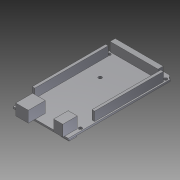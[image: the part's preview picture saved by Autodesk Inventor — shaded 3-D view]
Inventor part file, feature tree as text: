
AUTODESK INVENTOR PART (.ipt)
format: ipt  version: 2011 SP2 (Build 150309200, 309)  size: 225,792 bytes
history: native  units: mm
features: extrude x6, projected_geometry x5, sketch x3
ambient origin geometry x8: Origin, YZ Plane, XZ Plane, XY Plane, X Axis, Y Axis, Z Axis, Center Point
bodies: Solid1 (feature_tree)
feature tree (14):
  extrude  "Extrusion1"  Depth=1.7mm
  sketch  "Sketch3"  dims[d2=53.3mm d3=0.0mm d23=9.1mm]
  extrude  "Extrusion3"  Depth=9.1mm
  extrude  "Extrusion9"  Depth=16.4mm
  extrude  "Extrusion10"  Depth=12.2mm
  sketch  "Sketch7"  dims[d24=9.75mm d25=16.4mm d26=12.2mm d27=8.8mm d28=14.0mm d29=12.4mm d30=1.7mm d31=10.8mm d32=0.0mm d44=3.0mm d45=3.4mm d46=3.0mm d47=3.0mm d48=1.4mm d49=4.0mm d50=35.12mm d51=12.0mm d52=3.3mm d53=3.3mm d54=3.3mm d55=3.3mm d56=3.3mm d57=3.3mm d58=0.9mm d59=3.6mm d60=6.9mm d61=0.9mm d62=0.9mm d63=0.9mm d64=13.6mm d66=12.6mm d67=34.0mm d69=34.0mm d70=6.0mm d71=16.2mm d72=71.0mm d73=0.25mm d74=2.5mm d75=1.25mm d76=66.5mm d77=2.5mm d78=1.25mm d79=1.8mm d80=5.0mm d81=46.4mm d82=1.1mm d83=0.95mm d84=10.0mm d85=0.0mm d86=8.7mm d87=0.0mm d110=1.0mm d111=1.0mm d112=1.0mm d113=1.5mm d114=1.0mm d115=1.3mm d116=0.0mm d117=2.5mm d118=0.0mm]
  extrude  "Extrusion12"  Depth=8.8mm
  extrude  "Extrusion13"  Depth=14.0mm
  sketch  "Sketch1"  dims[d0=102.0mm d1=1.7mm]
  projected_geometry  "Projected Loop1"
  projected_geometry  "Projected Loop2"
  projected_geometry  "Projected Loop3"
  projected_geometry  "Projected Loop4"
  projected_geometry  "Projected Loop5"
